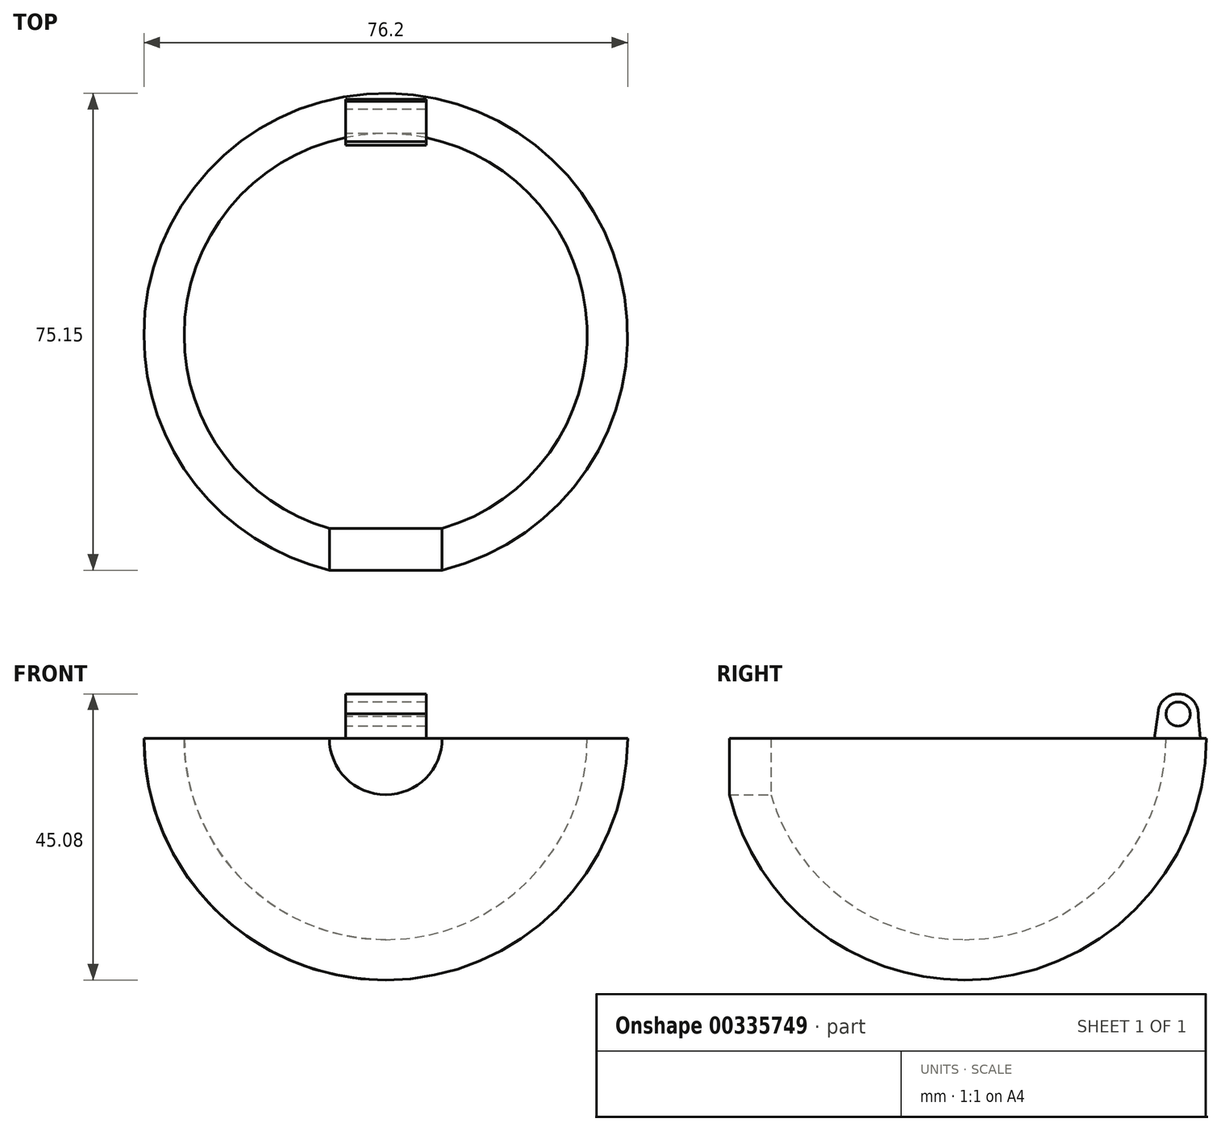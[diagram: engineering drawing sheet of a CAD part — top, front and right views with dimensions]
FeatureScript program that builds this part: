
annotation { "Feature Type Name" : "Feature", "Feature Type Description" : "" }
export const myFeature = defineFeature(function(context is Context, id is Id, definition is map)
    precondition{}
    {
        {
            var Q0;
            Q0=qCreatedBy(makeId("Front.planeOp"),FACE);
            var sketch = newSketch(context, id + "F0", { "sketchPlane" : qUnion([Q0])});
            skArc(sketch, "E0", {"start": v(-38.1, 0) * mm, "mid": v(-26.94, -26.94) * mm, "end": v(0, -38.1) * mm});
            skLineSegment(sketch, "E1", {"start": v(-38.1, 0) * mm, "end": v(-31.75, 0) * mm});
            skLineSegment(sketch, "E2", {"start": v(0, -31.75) * mm, "end": v(0, -38.1) * mm});
            skPoint(sketch, "E3.orphan", {"position": v(0, 38.1) * mm});
            skArc(sketch, "E4.0", {"start": v(-31.75, 0) * mm, "mid": v(-22.45, -22.45) * mm, "end": v(0, -31.75) * mm});
            skSolve(sketch);
        }
        {
            var Q0;
            Q0=makeQuery(id+"F0.imprint","IMPRINT",FACE,{"disambiguationData":[TD([[makeQuery(id+"F0.imprint","IMPRINT",EDGE,{"derivedFrom":sQuery(id+"F0.wireOp",EDGE,"E0")}),1.0]])]});
            var Q1;
            Q1=sQuery(id+"F0.wireOp",EDGE,"E2");
            revolve(context, id + "F1", {"entities" : qUnion([Q0]), "axis" : qUnion([Q1]), "revolveType" : RevolveType.FULL});
        }
        {
            var Q0;
            Q0=qCreatedBy(makeId("Front.planeOp"),FACE);
            var sketch = newSketch(context, id + "F2", { "sketchPlane" : qUnion([Q0])});
            skCircle(sketch, "E5", {"center": v(0, 0) * mm, "radius": 8.9 * mm});
            skSolve(sketch);
        }
        {
            var Q0;
            Q0 = qSketchRegion(id + "F2", true);
            extrude(context, id + "F3", {"entities" : qUnion([Q0]), "operationType" : NewBodyOperationType.REMOVE, "endBound" : BoundingType.THROUGH_ALL, "depth" : 25.4 * mm});
        }
        {
            var Q0;
            Q0=qCreatedBy(makeId("Right.planeOp"),FACE);
            var sketch = newSketch(context, id + "F4", { "sketchPlane" : qUnion([Q0])});
            skPoint(sketch, "E6.0", {"position": v(0, 0) * mm});
            skLineSegment(sketch, "E7.trimOffspring", {"start": v(31.75, 0) * mm, "end": v(38.1, 0) * mm});
            skPoint(sketch, "E8.0.3.end.orphan", {"position": v(-30.48, 0) * mm});
            skPoint(sketch, "E8.0.3.start.orphan", {"position": v(-37.05, 0) * mm});
            skPoint(sketch, "E8.0.2.end.orphan", {"position": v(-37.05, 0) * mm});
            skPoint(sketch, "E8.0.2.start.orphan", {"position": v(-30.48, 0) * mm});
            skCircle(sketch, "E9", {"center": v(33.65, 3.8) * mm, "radius": 1.9 * mm});
            skLineSegment(sketch, "E10", {"start": v(35.5, 4.25) * mm, "end": v(35.55, 3.66) * mm});
            skArc(sketch, "E11.0", {"start": v(36.8, 3.4) * mm, "mid": v(33.88, 6.98) * mm, "end": v(30.48, 3.85) * mm});
            skLineSegment(sketch, "E12", {"start": v(36.8, 3.4) * mm, "end": v(37.15, 0) * mm});
            skLineSegment(sketch, "E13", {"start": v(30.48, 3.85) * mm, "end": v(29.89, 0) * mm});
            skLineSegment(sketch, "E14", {"start": v(29.89, 0) * mm, "end": v(37.15, 0) * mm});
            skSolve(sketch);
        }
        {
            var Q0;
            Q0=makeQuery(id+"F4.imprint","IMPRINT",FACE,{"disambiguationData":[TD([[makeQuery(id+"F4.imprint","IMPRINT",EDGE,{"derivedFrom":sQuery(id+"F4.wireOp",EDGE,"E11.0")}),1.0]])]});
            extrude(context, id + "F5", {"entities" : qUnion([Q0]), "operationType" : NewBodyOperationType.ADD, "endBound" : BoundingType.SYMMETRIC, "depth" : 12.7 * mm});
        }
    });
